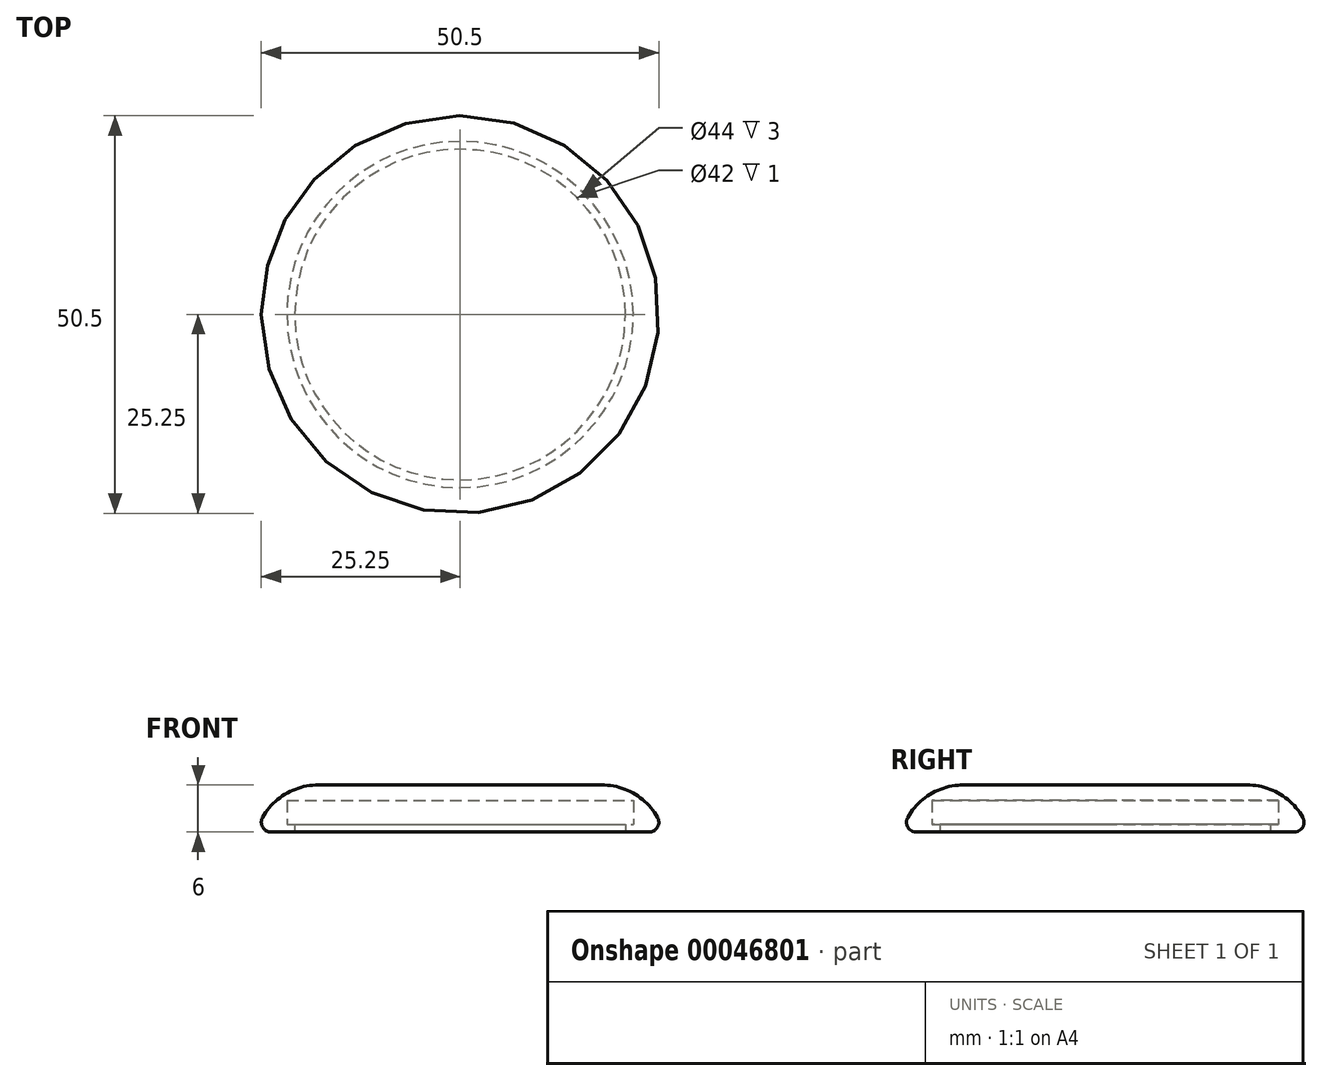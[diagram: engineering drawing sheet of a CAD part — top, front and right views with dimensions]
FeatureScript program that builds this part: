
annotation { "Feature Type Name" : "Feature", "Feature Type Description" : "" }
export const myFeature = defineFeature(function(context is Context, id is Id, definition is map)
    precondition{}
    {
        {
            var Q0;
            Q0=qCreatedBy(makeId("Front.planeOp"),FACE);
            var sketch = newSketch(context, id + "F0", { "sketchPlane" : qUnion([Q0])});
            skLineSegment(sketch, "E0", {"start": v(24, 0) * mm, "end": v(24, 1.87) * mm});
            skLineSegment(sketch, "E1", {"start": v(24, 1.87) * mm, "end": v(25.09, 1.87) * mm});
            skArc(sketch, "E2", {"start": v(24, 0) * mm, "mid": v(25.08, 0.62) * mm, "end": v(25.09, 1.87) * mm});
            skLineSegment(sketch, "E3", {"start": v(0, 4) * mm, "end": v(0, 6) * mm});
            skLineSegment(sketch, "E4", {"start": v(24, 0) * mm, "end": v(21, 0) * mm});
            skLineSegment(sketch, "E5", {"start": v(0, 6) * mm, "end": v(18, 6) * mm});
            skArc(sketch, "E6", {"start": v(25.09, 1.87) * mm, "mid": v(22.1, 4.9) * mm, "end": v(18, 6) * mm});
            skLineSegment(sketch, "E7", {"start": v(21, 0) * mm, "end": v(21, 1) * mm});
            skLineSegment(sketch, "E8", {"start": v(21, 1) * mm, "end": v(22, 1) * mm});
            skLineSegment(sketch, "E9", {"start": v(22, 1) * mm, "end": v(22, 4) * mm});
            skLineSegment(sketch, "E10", {"start": v(22, 4) * mm, "end": v(0, 4) * mm});
            skPoint(sketch, "E11.orphan", {"position": v(0, 0) * mm});
            skSolve(sketch);
        }
        {
            var Q0;
            Q0=makeQuery(id+"F0.imprint","IMPRINT",FACE,{"disambiguationData":[TD([[makeQuery(id+"F0.imprint","IMPRINT",EDGE,{"derivedFrom":sQuery(id+"F0.wireOp",EDGE,"E0")}),1.0]])]});
            var Q1;
            Q1=makeQuery(id+"F0.imprint","IMPRINT",FACE,{"disambiguationData":[TD([[makeQuery(id+"F0.imprint","IMPRINT",EDGE,{"derivedFrom":sQuery(id+"F0.wireOp",EDGE,"E0")}),-1.0]])]});
            var Q2;
            Q2=sQuery(id+"F0.wireOp",EDGE,"E3");
            revolve(context, id + "F1", {"entities" : qUnion([Q0, Q1]), "axis" : qUnion([Q2]), "revolveType" : RevolveType.FULL});
        }
    });
